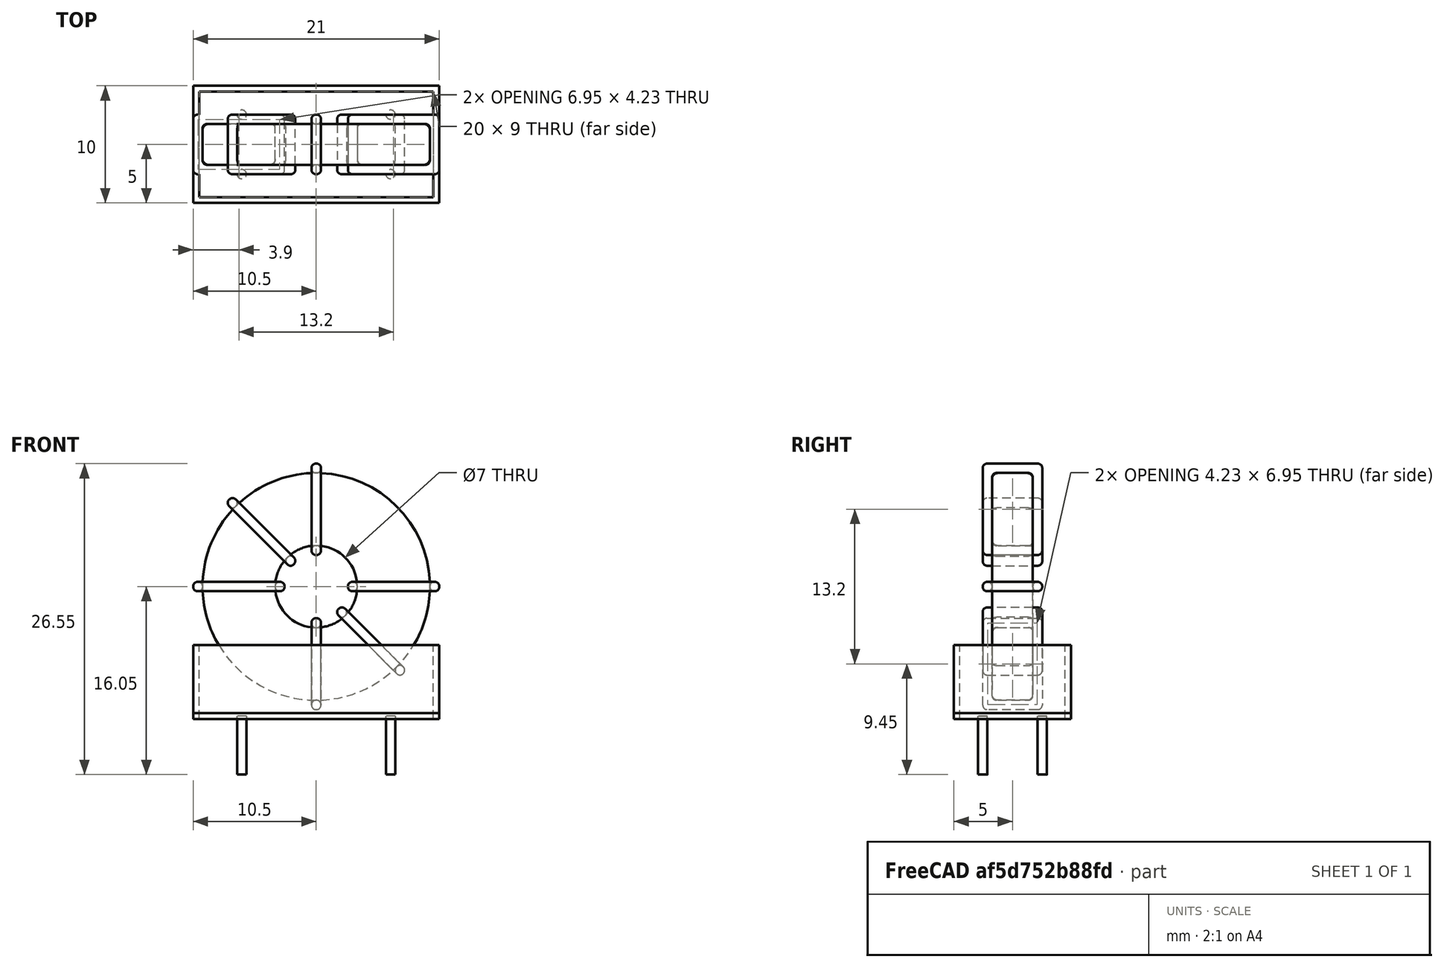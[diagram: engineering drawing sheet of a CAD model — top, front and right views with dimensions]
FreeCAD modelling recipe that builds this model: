
FCSTD DOCUMENT  (FreeCAD 0.16R6703 (Git))
Label: L_CommonModeChoke_Toroid_Vertical_L21.0mm_W10.0mm_Px5.08mm_Py12.70mm_muRATA_5100series
License: All rights reserved
LicenseURL: http://en.wikipedia.org/wiki/All_rights_reserved
objects: Sketcher::SketchObject×8, PartDesign::Pad×8, PartDesign::Fillet×5, Spreadsheet::Sheet×1
note: 29 computed .brp shape members not serialized (recipe doc carries the construction recipe); baked Part::Feature solids carry a one-line shape summary decoded from their .brp

FEATURE [Spreadsheet::Sheet] Spreadsheet  label="dimensions"
  cells = A1=Wx; B1(Wx)=21; C1(WW)=7; D1(iWx)=21; A2=Wy; B2(Wy)=5.08; D2(iWy)=10; A3=RM; B3(RMx)=5.08; C3(RMy)=12.7; A4=d_wire; B4(d_wire)=0.8; A5=H; B5(H)=31; A6=offsetx; B6(offsetx)=4.15
FEATURE [Sketcher::SketchObject] Sketch
  Placement = pos=(6.35,-2.54,0) rot=(1,0,0;1.5708rad)
  expr: Placement.Base.x = Spreadsheet.RMy / 2
  expr: Constraints[4] = Spreadsheet.WW / 2
  expr: Placement.Base.y = -Spreadsheet.RMx / 2
  expr: Constraints[0] = Spreadsheet.Wx / 2 - Spreadsheet.d_wire
  expr: Constraints[2] = Spreadsheet.Wx / 2 + Spreadsheet.d_wire + 0.5
  sketch-geometry (2):
    g0: Circle CenterX=0 CenterY=11.8 CenterZ=0 NormalX=0 NormalY=0 NormalZ=1 Radius=9.7
    g1: Circle CenterX=0 CenterY=11.8 CenterZ=0 NormalX=0 NormalY=0 NormalZ=1 Radius=3.5
  constraints (5):
    c: Radius(g0) = 9.7
    c: DistanceX(g-1,g0) = 0
    c: DistanceY(g-1,g0) = 11.8
    c: Coincident(g1,g0)
    c: Radius(g1) = 3.5
FEATURE [PartDesign::Pad] Pad
  Length = 3.48
  Length2 = 100
  Midplane = true
  Placement = pos=(6.35,-2.54,0) rot=(1,0,0;1.5708rad)
  Sketch = -> Sketch
  Type = 0
  expr: Length = Spreadsheet.Wy - 2 * Spreadsheet.d_wire
FEATURE [Sketcher::SketchObject] Sketch001
  Placement = pos=(0,0,0.75) rot=(0,0,1;0rad)
  expr: Constraints[4] = Spreadsheet.RMy
  expr: Constraints[2] = -Spreadsheet.RMx
  expr: Constraints[1] = Spreadsheet.d_wire / 2
  sketch-geometry (4):
    g0: Circle CenterX=0 CenterY=0 CenterZ=0 NormalX=0 NormalY=0 NormalZ=1 Radius=0.4
    g1: Circle CenterX=12.7 CenterY=-5.08 CenterZ=0 NormalX=0 NormalY=0 NormalZ=1 Radius=0.4
    g2: Circle CenterX=0 CenterY=-5.08 CenterZ=0 NormalX=0 NormalY=0 NormalZ=1 Radius=0.4
    g3: Circle CenterX=12.7 CenterY=0 CenterZ=0 NormalX=0 NormalY=0 NormalZ=1 Radius=0.4
  constraints (11):
    c: Equal(g0,g1)
    c: Radius(g0) = 0.4
    c: DistanceY(g-1,g1) = -5.08
    c: Coincident(g0,g-1)
    c: DistanceX(g-1,g1) = 12.7
    c: PointOnObject(g2,g-2)
    c: DistanceY(g-1,g3) = 0
    c: DistanceY(g2,g1) = 0
    c: DistanceX(g3,g1) = 0
    c: Equal(g3,g2)
    c: Equal(g2,g1)
FEATURE [PartDesign::Pad] Pad001
  Length = 5
  Length2 = 0
  Placement = pos=(0,0,0.75) rot=(0,0,1;0rad)
  Reversed = true
  Sketch = -> Sketch001
  Type = 0
FEATURE [PartDesign::Fillet] Fillet
  Base = -> Pad [Edge6,Edge3,Edge2]
  Placement = pos=(6.35,-2.54,0) rot=(1,0,0;1.5708rad)
  Radius = 0.5
FEATURE [Sketcher::SketchObject] Sketch003
  Placement = pos=(6.35,0,11.8) rot=(1,0,0;3.14159rad)
  expr: Placement.Base.x = Spreadsheet.RMy / 2
  expr: Constraints[18] = Spreadsheet.d_wire
  expr: Constraints[16] = Spreadsheet.d_wire
  expr: Constraints[19] = Spreadsheet.d_wire
  expr: Constraints[17] = Spreadsheet.d_wire
  expr: Placement.Base.y = -1 * (Spreadsheet.RMx - Spreadsheet.Wy) / 2
  expr: Constraints[21] = (Spreadsheet.Wx - Spreadsheet.WW) / 2 - Spreadsheet.d_wire
  expr: Constraints[22] = Spreadsheet.Wx / 2 - Spreadsheet.d_wire
  expr: Constraints[43] = Spreadsheet.d_wire
  expr: Constraints[48] = Spreadsheet.Wx - Spreadsheet.d_wire * 2
  expr: Constraints[49] = Spreadsheet.Wy
  expr: Placement.Base.z = Spreadsheet.Wx / 2 + Spreadsheet.d_wire + 0.5
  sketch-geometry (16):
    g0: LineSegment StartX=-2.7 StartY=0 StartZ=0 EndX=-10.5 EndY=0 EndZ=0
    g1: LineSegment StartX=-10.5 StartY=0 StartZ=0 EndX=-10.5 EndY=5.08 EndZ=0
    g2: LineSegment StartX=-10.5 StartY=5.08 StartZ=0 EndX=-2.7 EndY=5.08 EndZ=0
    g3: LineSegment StartX=-2.7 StartY=5.08 StartZ=0 EndX=-2.7 EndY=0 EndZ=0
    g4: LineSegment StartX=-9.7 StartY=4.28 StartZ=0 EndX=-3.5 EndY=4.28 EndZ=0
    g5: LineSegment StartX=-3.5 StartY=4.28 StartZ=0 EndX=-3.5 EndY=0.8 EndZ=0
    g6: LineSegment StartX=-3.5 StartY=0.8 StartZ=0 EndX=-9.7 EndY=0.8 EndZ=0
    g7: LineSegment StartX=-9.7 StartY=0.8 StartZ=0 EndX=-9.7 EndY=4.28 EndZ=0
    g8: LineSegment StartX=2.7 StartY=5.08 StartZ=0 EndX=10.5 EndY=5.08 EndZ=0
    g9: LineSegment StartX=10.5 StartY=5.08 StartZ=0 EndX=10.5 EndY=0 EndZ=0
    g10: LineSegment StartX=10.5 StartY=0 StartZ=0 EndX=2.7 EndY=0 EndZ=0
    g11: LineSegment StartX=2.7 StartY=0 StartZ=0 EndX=2.7 EndY=5.08 EndZ=0
    g12: LineSegment StartX=3.5 StartY=4.28 StartZ=0 EndX=9.7 EndY=4.28 EndZ=0
    g13: LineSegment StartX=9.7 StartY=4.28 StartZ=0 EndX=9.7 EndY=0.8 EndZ=0
    g14: LineSegment StartX=9.7 StartY=0.8 StartZ=0 EndX=3.5 EndY=0.8 EndZ=0
    g15: LineSegment StartX=3.5 StartY=0.8 StartZ=0 EndX=3.5 EndY=4.28 EndZ=0
  constraints (50):
    c: Horizontal(g0)
    c: Coincident(g1,g0)
    c: Vertical(g1)
    c: Coincident(g2,g1)
    c: Horizontal(g2)
    c: Coincident(g3,g2)
    c: Coincident(g3,g0)
    c: Vertical(g3)
    c: Coincident(g4,g5)
    c: Coincident(g5,g6)
    c: Coincident(g6,g7)
    c: Coincident(g7,g4)
    c: Horizontal(g4)
    c: Horizontal(g6)
    c: Vertical(g5)
    c: Vertical(g7)
    c: DistanceX(g1,g4) = 0.8
    c: DistanceY(g4,g1) = 0.8
    c: DistanceX(g5,g0) = 0.8
    c: DistanceY(g0,g5) = 0.8
    c: DistanceY(g-1,g0) = 0
    c: DistanceX(g6,g6) = 6.2
    c: DistanceX(g6,g-1) = 9.7
    c: Coincident(g8,g9)
    c: Coincident(g9,g10)
    c: Coincident(g10,g11)
    c: Coincident(g11,g8)
    c: Horizontal(g8)
    c: Horizontal(g10)
    c: Vertical(g9)
    c: Vertical(g11)
    c: Coincident(g12,g13)
    c: Coincident(g13,g14)
    c: Coincident(g14,g15)
    c: Coincident(g15,g12)
    c: Horizontal(g12)
    c: Horizontal(g14)
    c: Vertical(g13)
    c: Vertical(g15)
    c: DistanceY(g8,g2) = 0
    c: DistanceY(g10,g0) = 0
    c: DistanceY(g14,g5) = 0
    c: DistanceY(g12,g4) = 0
    c: DistanceX(g8,g12) = 0.8
    c: Equal(g8,g2)
    c: Equal(g12,g4)
    c: Equal(g9,g1)
    c: Equal(g13,g7)
    c: DistanceX(g4,g12) = 19.4
    c: DistanceY(g0,g1) = 5.08
FEATURE [PartDesign::Pad] Pad002
  Length = 0.8
  Length2 = 100
  Midplane = true
  Placement = pos=(6.35,0,11.8) rot=(1,0,0;3.14159rad)
  Sketch = -> Sketch003
  Type = 0
  expr: Length = Spreadsheet.d_wire
FEATURE [PartDesign::Fillet] Fillet001
  Base = -> Pad002 [Edge38,Edge41,Edge42,Edge43,Edge29,Edge32,Edge33,Edge34,Edge25,Edge35,Edge36,Edge13,Edge14,Edge15,Edge16,Edge17,Edge18,Edge19,Edge1,Edge2,Edge3,Edge4,Edge5,Edge6,Edge7,Edge37,Edge39,Edge40,Edge20,Edge23,Edge24,Edge21,Edge22,Edge8,Edge9,Edge10,Edge11,Edge12,Edge26,Edge27,+8 more]
  Placement = pos=(6.35,0,11.8) rot=(1,0,0;3.14159rad)
  Radius = 0.376
  expr: Radius = Spreadsheet.d_wire * 0.47
FEATURE [Sketcher::SketchObject] Sketch004
  Placement = pos=(6.35,0,11.8) rot=(0.92388,0,0.382683;3.14159rad)
  expr: Placement.Base.x = Spreadsheet.RMy / 2
  expr: Constraints[18] = Spreadsheet.d_wire
  expr: Constraints[16] = Spreadsheet.d_wire
  expr: Constraints[19] = Spreadsheet.d_wire
  expr: Constraints[17] = Spreadsheet.d_wire
  expr: Placement.Base.y = -1 * (Spreadsheet.RMx - Spreadsheet.Wy) / 2
  expr: Constraints[21] = (Spreadsheet.Wx - Spreadsheet.WW) / 2 - Spreadsheet.d_wire
  expr: Constraints[22] = Spreadsheet.Wx / 2 - Spreadsheet.d_wire
  expr: Constraints[43] = Spreadsheet.d_wire
  expr: Constraints[48] = Spreadsheet.Wx - 2 * Spreadsheet.d_wire
  expr: Constraints[49] = Spreadsheet.Wy
  expr: Placement.Base.z = Spreadsheet.Wx / 2 + Spreadsheet.d_wire + 0.5
  sketch-geometry (16):
    g0: LineSegment StartX=-2.7 StartY=0 StartZ=0 EndX=-10.5 EndY=0 EndZ=0
    g1: LineSegment StartX=-10.5 StartY=0 StartZ=0 EndX=-10.5 EndY=5.08 EndZ=0
    g2: LineSegment StartX=-10.5 StartY=5.08 StartZ=0 EndX=-2.7 EndY=5.08 EndZ=0
    g3: LineSegment StartX=-2.7 StartY=5.08 StartZ=0 EndX=-2.7 EndY=0 EndZ=0
    g4: LineSegment StartX=-9.7 StartY=4.28 StartZ=0 EndX=-3.5 EndY=4.28 EndZ=0
    g5: LineSegment StartX=-3.5 StartY=4.28 StartZ=0 EndX=-3.5 EndY=0.8 EndZ=0
    g6: LineSegment StartX=-3.5 StartY=0.8 StartZ=0 EndX=-9.7 EndY=0.8 EndZ=0
    g7: LineSegment StartX=-9.7 StartY=0.8 StartZ=0 EndX=-9.7 EndY=4.28 EndZ=0
    g8: LineSegment StartX=2.7 StartY=5.08 StartZ=0 EndX=10.5 EndY=5.08 EndZ=0
    g9: LineSegment StartX=10.5 StartY=5.08 StartZ=0 EndX=10.5 EndY=0 EndZ=0
    g10: LineSegment StartX=10.5 StartY=0 StartZ=0 EndX=2.7 EndY=0 EndZ=0
    g11: LineSegment StartX=2.7 StartY=0 StartZ=0 EndX=2.7 EndY=5.08 EndZ=0
    g12: LineSegment StartX=3.5 StartY=4.28 StartZ=0 EndX=9.7 EndY=4.28 EndZ=0
    g13: LineSegment StartX=9.7 StartY=4.28 StartZ=0 EndX=9.7 EndY=0.8 EndZ=0
    g14: LineSegment StartX=9.7 StartY=0.8 StartZ=0 EndX=3.5 EndY=0.8 EndZ=0
    g15: LineSegment StartX=3.5 StartY=0.8 StartZ=0 EndX=3.5 EndY=4.28 EndZ=0
  constraints (50):
    c: Horizontal(g0)
    c: Coincident(g1,g0)
    c: Vertical(g1)
    c: Coincident(g2,g1)
    c: Horizontal(g2)
    c: Coincident(g3,g2)
    c: Coincident(g3,g0)
    c: Vertical(g3)
    c: Coincident(g4,g5)
    c: Coincident(g5,g6)
    c: Coincident(g6,g7)
    c: Coincident(g7,g4)
    c: Horizontal(g4)
    c: Horizontal(g6)
    c: Vertical(g5)
    c: Vertical(g7)
    c: DistanceX(g1,g4) = 0.8
    c: DistanceY(g4,g1) = 0.8
    c: DistanceX(g5,g0) = 0.8
    c: DistanceY(g0,g5) = 0.8
    c: DistanceY(g-1,g0) = 0
    c: DistanceX(g6,g6) = 6.2
    c: DistanceX(g6,g-1) = 9.7
    c: Coincident(g8,g9)
    c: Coincident(g9,g10)
    c: Coincident(g10,g11)
    c: Coincident(g11,g8)
    c: Horizontal(g8)
    c: Horizontal(g10)
    c: Vertical(g9)
    c: Vertical(g11)
    c: Coincident(g12,g13)
    c: Coincident(g13,g14)
    c: Coincident(g14,g15)
    c: Coincident(g15,g12)
    c: Horizontal(g12)
    c: Horizontal(g14)
    c: Vertical(g13)
    c: Vertical(g15)
    c: DistanceY(g8,g2) = 0
    c: DistanceY(g10,g0) = 0
    c: DistanceY(g14,g5) = 0
    c: DistanceY(g12,g4) = 0
    c: DistanceX(g8,g12) = 0.8
    c: Equal(g8,g2)
    c: Equal(g12,g4)
    c: Equal(g9,g1)
    c: Equal(g13,g7)
    c: DistanceX(g4,g12) = 19.4
    c: DistanceY(g0,g1) = 5.08
FEATURE [PartDesign::Pad] Pad003
  Length = 0.8
  Length2 = 100
  Midplane = true
  Placement = pos=(6.35,0,11.8) rot=(0.92388,0,0.382683;3.14159rad)
  Sketch = -> Sketch004
  Type = 0
  expr: Length = Spreadsheet.d_wire
FEATURE [PartDesign::Fillet] Fillet002
  Base = -> Pad003 [Edge38,Edge41,Edge42,Edge43,Edge29,Edge32,Edge33,Edge34,Edge25,Edge35,Edge36,Edge13,Edge14,Edge15,Edge16,Edge17,Edge18,Edge19,Edge1,Edge2,Edge3,Edge4,Edge5,Edge6,Edge7,Edge37,Edge39,Edge40,Edge20,Edge23,Edge24,Edge21,Edge22,Edge8,Edge9,Edge10,Edge11,Edge12,Edge26,Edge27,+8 more]
  Placement = pos=(6.35,0,11.8) rot=(0.92388,0,0.382683;3.14159rad)
  Radius = 0.376
  expr: Radius = Spreadsheet.d_wire * 0.47
FEATURE [Sketcher::SketchObject] Sketch005
  Placement = pos=(6.35,0,11.8) rot=(0.92388,0,-0.382683;3.14159rad)
  expr: Placement.Base.x = Spreadsheet.RMy / 2
  expr: Constraints[18] = Spreadsheet.d_wire
  expr: Constraints[16] = Spreadsheet.d_wire
  expr: Constraints[19] = Spreadsheet.d_wire
  expr: Constraints[17] = Spreadsheet.d_wire
  expr: Placement.Base.y = -1 * (Spreadsheet.RMx - Spreadsheet.Wy) / 2
  expr: Constraints[21] = (Spreadsheet.Wx - Spreadsheet.WW) / 2 - Spreadsheet.d_wire
  expr: Constraints[22] = Spreadsheet.Wx / 2 - Spreadsheet.d_wire
  expr: Constraints[43] = Spreadsheet.d_wire
  expr: Constraints[48] = Spreadsheet.Wx - 2 * Spreadsheet.d_wire
  expr: Constraints[49] = Spreadsheet.Wy
  expr: Placement.Base.z = Spreadsheet.Wx / 2 + Spreadsheet.d_wire + 0.5
  sketch-geometry (16):
    g0: LineSegment StartX=-2.7 StartY=0 StartZ=0 EndX=-10.5 EndY=0 EndZ=0
    g1: LineSegment StartX=-10.5 StartY=0 StartZ=0 EndX=-10.5 EndY=5.08 EndZ=0
    g2: LineSegment StartX=-10.5 StartY=5.08 StartZ=0 EndX=-2.7 EndY=5.08 EndZ=0
    g3: LineSegment StartX=-2.7 StartY=5.08 StartZ=0 EndX=-2.7 EndY=0 EndZ=0
    g4: LineSegment StartX=-9.7 StartY=4.28 StartZ=0 EndX=-3.5 EndY=4.28 EndZ=0
    g5: LineSegment StartX=-3.5 StartY=4.28 StartZ=0 EndX=-3.5 EndY=0.8 EndZ=0
    g6: LineSegment StartX=-3.5 StartY=0.8 StartZ=0 EndX=-9.7 EndY=0.8 EndZ=0
    g7: LineSegment StartX=-9.7 StartY=0.8 StartZ=0 EndX=-9.7 EndY=4.28 EndZ=0
    g8: LineSegment StartX=2.7 StartY=5.08 StartZ=0 EndX=10.5 EndY=5.08 EndZ=0
    g9: LineSegment StartX=10.5 StartY=5.08 StartZ=0 EndX=10.5 EndY=0 EndZ=0
    g10: LineSegment StartX=10.5 StartY=0 StartZ=0 EndX=2.7 EndY=0 EndZ=0
    g11: LineSegment StartX=2.7 StartY=0 StartZ=0 EndX=2.7 EndY=5.08 EndZ=0
    g12: LineSegment StartX=3.5 StartY=4.28 StartZ=0 EndX=9.7 EndY=4.28 EndZ=0
    g13: LineSegment StartX=9.7 StartY=4.28 StartZ=0 EndX=9.7 EndY=0.8 EndZ=0
    g14: LineSegment StartX=9.7 StartY=0.8 StartZ=0 EndX=3.5 EndY=0.8 EndZ=0
    g15: LineSegment StartX=3.5 StartY=0.8 StartZ=0 EndX=3.5 EndY=4.28 EndZ=0
  constraints (50):
    c: Horizontal(g0)
    c: Coincident(g1,g0)
    c: Vertical(g1)
    c: Coincident(g2,g1)
    c: Horizontal(g2)
    c: Coincident(g3,g2)
    c: Coincident(g3,g0)
    c: Vertical(g3)
    c: Coincident(g4,g5)
    c: Coincident(g5,g6)
    c: Coincident(g6,g7)
    c: Coincident(g7,g4)
    c: Horizontal(g4)
    c: Horizontal(g6)
    c: Vertical(g5)
    c: Vertical(g7)
    c: DistanceX(g1,g4) = 0.8
    c: DistanceY(g4,g1) = 0.8
    c: DistanceX(g5,g0) = 0.8
    c: DistanceY(g0,g5) = 0.8
    c: DistanceY(g-1,g0) = 0
    c: DistanceX(g6,g6) = 6.2
    c: DistanceX(g6,g-1) = 9.7
    c: Coincident(g8,g9)
    c: Coincident(g9,g10)
    c: Coincident(g10,g11)
    c: Coincident(g11,g8)
    c: Horizontal(g8)
    c: Horizontal(g10)
    c: Vertical(g9)
    c: Vertical(g11)
    c: Coincident(g12,g13)
    c: Coincident(g13,g14)
    c: Coincident(g14,g15)
    c: Coincident(g15,g12)
    c: Horizontal(g12)
    c: Horizontal(g14)
    c: Vertical(g13)
    c: Vertical(g15)
    c: DistanceY(g8,g2) = 0
    c: DistanceY(g10,g0) = 0
    c: DistanceY(g14,g5) = 0
    c: DistanceY(g12,g4) = 0
    c: DistanceX(g8,g12) = 0.8
    c: Equal(g8,g2)
    c: Equal(g12,g4)
    c: Equal(g9,g1)
    c: Equal(g13,g7)
    c: DistanceX(g4,g12) = 19.4
    c: DistanceY(g0,g1) = 5.08
FEATURE [PartDesign::Pad] Pad004
  Length = 0.8
  Length2 = 100
  Midplane = true
  Placement = pos=(6.35,0,11.8) rot=(0.92388,0,-0.382683;3.14159rad)
  Sketch = -> Sketch005
  Type = 0
  expr: Length = Spreadsheet.d_wire
FEATURE [PartDesign::Fillet] Fillet003
  Base = -> Pad004 [Edge38,Edge41,Edge42,Edge43,Edge29,Edge32,Edge33,Edge34,Edge25,Edge35,Edge36,Edge13,Edge14,Edge15,Edge16,Edge17,Edge18,Edge19,Edge1,Edge2,Edge3,Edge4,Edge5,Edge6,Edge7,Edge37,Edge39,Edge40,Edge20,Edge23,Edge24,Edge21,Edge22,Edge8,Edge9,Edge10,Edge11,Edge12,Edge26,Edge27,+8 more]
  Placement = pos=(6.35,0,11.8) rot=(0.92388,0,-0.382683;3.14159rad)
  Radius = 0.376
  expr: Radius = Spreadsheet.d_wire * 0.47
FEATURE [Sketcher::SketchObject] Sketch006
  Placement = pos=(6.35,0,11.8) rot=(0.707107,0,0.707107;3.14159rad)
  expr: Placement.Base.x = Spreadsheet.RMy / 2
  expr: Constraints[18] = Spreadsheet.d_wire
  expr: Constraints[16] = Spreadsheet.d_wire
  expr: Constraints[19] = Spreadsheet.d_wire
  expr: Constraints[17] = Spreadsheet.d_wire
  expr: Placement.Base.y = -1 * (Spreadsheet.RMx - Spreadsheet.Wy) / 2
  expr: Constraints[21] = (Spreadsheet.Wx - Spreadsheet.WW) / 2 - Spreadsheet.d_wire
  expr: Constraints[22] = Spreadsheet.Wx / 2 - Spreadsheet.d_wire
  expr: Constraints[43] = Spreadsheet.d_wire
  expr: Constraints[48] = Spreadsheet.Wx - Spreadsheet.d_wire * 2
  expr: Constraints[49] = Spreadsheet.Wy
  expr: Placement.Base.z = Spreadsheet.Wx / 2 + Spreadsheet.d_wire + 0.5
  sketch-geometry (16):
    g0: LineSegment StartX=-2.7 StartY=0 StartZ=0 EndX=-10.5 EndY=0 EndZ=0
    g1: LineSegment StartX=-10.5 StartY=0 StartZ=0 EndX=-10.5 EndY=5.08 EndZ=0
    g2: LineSegment StartX=-10.5 StartY=5.08 StartZ=0 EndX=-2.7 EndY=5.08 EndZ=0
    g3: LineSegment StartX=-2.7 StartY=5.08 StartZ=0 EndX=-2.7 EndY=0 EndZ=0
    g4: LineSegment StartX=-9.7 StartY=4.28 StartZ=0 EndX=-3.5 EndY=4.28 EndZ=0
    g5: LineSegment StartX=-3.5 StartY=4.28 StartZ=0 EndX=-3.5 EndY=0.8 EndZ=0
    g6: LineSegment StartX=-3.5 StartY=0.8 StartZ=0 EndX=-9.7 EndY=0.8 EndZ=0
    g7: LineSegment StartX=-9.7 StartY=0.8 StartZ=0 EndX=-9.7 EndY=4.28 EndZ=0
    g8: LineSegment StartX=2.7 StartY=5.08 StartZ=0 EndX=10.5 EndY=5.08 EndZ=0
    g9: LineSegment StartX=10.5 StartY=5.08 StartZ=0 EndX=10.5 EndY=0 EndZ=0
    g10: LineSegment StartX=10.5 StartY=0 StartZ=0 EndX=2.7 EndY=0 EndZ=0
    g11: LineSegment StartX=2.7 StartY=0 StartZ=0 EndX=2.7 EndY=5.08 EndZ=0
    g12: LineSegment StartX=3.5 StartY=4.28 StartZ=0 EndX=9.7 EndY=4.28 EndZ=0
    g13: LineSegment StartX=9.7 StartY=4.28 StartZ=0 EndX=9.7 EndY=0.8 EndZ=0
    g14: LineSegment StartX=9.7 StartY=0.8 StartZ=0 EndX=3.5 EndY=0.8 EndZ=0
    g15: LineSegment StartX=3.5 StartY=0.8 StartZ=0 EndX=3.5 EndY=4.28 EndZ=0
  constraints (50):
    c: Horizontal(g0)
    c: Coincident(g1,g0)
    c: Vertical(g1)
    c: Coincident(g2,g1)
    c: Horizontal(g2)
    c: Coincident(g3,g2)
    c: Coincident(g3,g0)
    c: Vertical(g3)
    c: Coincident(g4,g5)
    c: Coincident(g5,g6)
    c: Coincident(g6,g7)
    c: Coincident(g7,g4)
    c: Horizontal(g4)
    c: Horizontal(g6)
    c: Vertical(g5)
    c: Vertical(g7)
    c: DistanceX(g1,g4) = 0.8
    c: DistanceY(g4,g1) = 0.8
    c: DistanceX(g5,g0) = 0.8
    c: DistanceY(g0,g5) = 0.8
    c: DistanceY(g-1,g0) = 0
    c: DistanceX(g6,g6) = 6.2
    c: DistanceX(g6,g-1) = 9.7
    c: Coincident(g8,g9)
    c: Coincident(g9,g10)
    c: Coincident(g10,g11)
    c: Coincident(g11,g8)
    c: Horizontal(g8)
    c: Horizontal(g10)
    c: Vertical(g9)
    c: Vertical(g11)
    c: Coincident(g12,g13)
    c: Coincident(g13,g14)
    c: Coincident(g14,g15)
    c: Coincident(g15,g12)
    c: Horizontal(g12)
    c: Horizontal(g14)
    c: Vertical(g13)
    c: Vertical(g15)
    c: DistanceY(g8,g2) = 0
    c: DistanceY(g10,g0) = 0
    c: DistanceY(g14,g5) = 0
    c: DistanceY(g12,g4) = 0
    c: DistanceX(g8,g12) = 0.8
    c: Equal(g8,g2)
    c: Equal(g12,g4)
    c: Equal(g9,g1)
    c: Equal(g13,g7)
    c: DistanceX(g4,g12) = 19.4
    c: DistanceY(g0,g1) = 5.08
FEATURE [PartDesign::Pad] Pad005
  Length = 0.8
  Length2 = 100
  Midplane = true
  Placement = pos=(6.35,0,11.8) rot=(0.707107,0,0.707107;3.14159rad)
  Sketch = -> Sketch006
  Type = 0
  expr: Length = Spreadsheet.d_wire
FEATURE [PartDesign::Fillet] Fillet004
  Base = -> Pad005 [Edge38,Edge41,Edge42,Edge43,Edge29,Edge32,Edge33,Edge34,Edge25,Edge35,Edge36,Edge13,Edge14,Edge15,Edge16,Edge17,Edge18,Edge19,Edge1,Edge2,Edge3,Edge4,Edge5,Edge6,Edge7,Edge37,Edge39,Edge40,Edge20,Edge23,Edge24,Edge21,Edge22,Edge8,Edge9,Edge10,Edge11,Edge12,Edge26,Edge27,+8 more]
  Placement = pos=(6.35,0,11.8) rot=(0.707107,0,0.707107;3.14159rad)
  Radius = 0.376
  expr: Radius = Spreadsheet.d_wire * 0.47
FEATURE [Sketcher::SketchObject] Sketch007
  Placement = pos=(6.35,0,0.5) rot=(0,0,1;0rad)
  expr: Placement.Base.x = Spreadsheet.RMy / 2
  expr: Placement.Base.z = 0.5
  expr: Constraints[11] = Spreadsheet.iWx / 2
  expr: Constraints[10] = (Spreadsheet.iWy - Spreadsheet.RMx) / 2
  expr: Constraints[9] = Spreadsheet.iWy
  expr: Constraints[8] = Spreadsheet.iWx
  sketch-geometry (4):
    g0: LineSegment StartX=-10.5 StartY=2.46 StartZ=0 EndX=10.5 EndY=2.46 EndZ=0
    g1: LineSegment StartX=10.5 StartY=2.46 StartZ=0 EndX=10.5 EndY=-7.54 EndZ=0
    g2: LineSegment StartX=10.5 StartY=-7.54 StartZ=0 EndX=-10.5 EndY=-7.54 EndZ=0
    g3: LineSegment StartX=-10.5 StartY=-7.54 StartZ=0 EndX=-10.5 EndY=2.46 EndZ=0
  constraints (12):
    c: Coincident(g0,g1)
    c: Coincident(g1,g2)
    c: Coincident(g2,g3)
    c: Coincident(g3,g0)
    c: Horizontal(g0)
    c: Horizontal(g2)
    c: Vertical(g1)
    c: Vertical(g3)
    c: DistanceX(g0,g0) = 21
    c: DistanceY(g3,g3) = 10
    c: DistanceY(g-1,g0) = 2.46
    c: DistanceX(g0,g-1) = 10.5
FEATURE [PartDesign::Pad] Pad006
  Length = 0.5
  Length2 = 100
  Placement = pos=(6.35,0,0.5) rot=(0,0,1;0rad)
  Sketch = -> Sketch007
  Type = 0
FEATURE [Sketcher::SketchObject] Sketch008
  Placement = pos=(6.35,0,0.5) rot=(0,0,1;0rad)
  expr: Placement.Base.x = Spreadsheet.RMy / 2
  expr: Constraints[8] = Spreadsheet.iWx
  expr: Constraints[9] = Spreadsheet.iWy
  expr: Constraints[10] = (Spreadsheet.iWy - Spreadsheet.RMx) / 2
  expr: Placement.Base.z = 0.5
  expr: Constraints[21] = 0.5
  expr: Constraints[11] = Spreadsheet.iWx / 2
  sketch-geometry (8):
    g0: LineSegment StartX=-10.5 StartY=2.46 StartZ=0 EndX=10.5 EndY=2.46 EndZ=0
    g1: LineSegment StartX=10.5 StartY=2.46 StartZ=0 EndX=10.5 EndY=-7.54 EndZ=0
    g2: LineSegment StartX=10.5 StartY=-7.54 StartZ=0 EndX=-10.5 EndY=-7.54 EndZ=0
    g3: LineSegment StartX=-10.5 StartY=-7.54 StartZ=0 EndX=-10.5 EndY=2.46 EndZ=0
    g4: LineSegment StartX=-10 StartY=1.96 StartZ=0 EndX=10 EndY=1.96 EndZ=0
    g5: LineSegment StartX=10 StartY=1.96 StartZ=0 EndX=10 EndY=-7.04 EndZ=0
    g6: LineSegment StartX=10 StartY=-7.04 StartZ=0 EndX=-10 EndY=-7.04 EndZ=0
    g7: LineSegment StartX=-10 StartY=-7.04 StartZ=0 EndX=-10 EndY=1.96 EndZ=0
  constraints (24):
    c: Coincident(g0,g1)
    c: Coincident(g1,g2)
    c: Coincident(g2,g3)
    c: Coincident(g3,g0)
    c: Horizontal(g0)
    c: Horizontal(g2)
    c: Vertical(g1)
    c: Vertical(g3)
    c: DistanceX(g0,g0) = 21
    c: DistanceY(g3,g3) = 10
    c: DistanceY(g-1,g0) = 2.46
    c: DistanceX(g0,g-1) = 10.5
    c: Coincident(g4,g5)
    c: Coincident(g5,g6)
    c: Coincident(g6,g7)
    c: Coincident(g7,g4)
    c: Horizontal(g4)
    c: Horizontal(g6)
    c: Vertical(g5)
    c: Vertical(g7)
    c: DistanceX(g5,g1) = 0.5
    c: DistanceY(g1,g5) = 0.5
    c: DistanceX(g0,g4) = 0.5
    c: DistanceY(g4,g0) = 0.5
FEATURE [PartDesign::Pad] Pad007
  Length = 6.3
  Length2 = 100
  Placement = pos=(6.35,0,0.5) rot=(0,0,1;0rad)
  Sketch = -> Sketch008
  Type = 0
  expr: Length = Spreadsheet.Wx * 0.3
